# Revit family: Hitachi_RAS-50YHA3_RAS-60YHA3_VER2_0813
name_source: partatom
category: Mechanical Equipment
revit_build: Autodesk Revit 2013 (Build: 20120221_2030(x64)
units: mm (PartAtom-declared; Revit-internal decimal feet)

## types (2) — shared parameters
Dehumidifying Capacity = 2.8 l/h
Depth = 207 mm  [stored 0.679134 ft]
Height = 295 mm  [stored 0.967848 ft]
Manufacturer = Hitachi
Pip Connection Size - Liquid = 6.40 mm
Pipe Connection Size - Gas = 12.70 mm
Pipe Length (min./max.) = 3m to 30m
URL = www.temperzone.biz
Weight (kg) = 11
Width = 1030 mm  [stored 3.37927 ft]

## per-type parameters (varying)
| type | Cooling Capacity | Cooling Range (kW) | Description | Energy Star | Heating Capacity | Heating Range (kW) | Model - Outdoor | Pipe Height (max.) |
| RAS-60YHA3 | 6 kW | 0.9 kW to 6.8 kW | Hitachi Wall Mounted 6.0kW Heatpump RAS-60YHA3 | No | 7 kW | 0.9 kW to 7.5 kW | RAC-60YHA3 | 20m |
| RAS-50YHA3 | 5 kW | 0.9 kW to 5.8 kW | Hitachi Wall Mounted 5.0kW Heatpump RAS-50YHA3 | Yes | 6 kW | 0.9 kW to 6.8 kW | RAC-50YHA3 | 10m |

note: column(s) folded — value = type name in every type: Model

note: [stored X ft] marks values corroborated as IEEE doubles in the binary element streams (Revit-internal decimal feet)

## geometry (parser evidence)
native form markers: Blend x4, Sweep x3
no freeform markers — native parametric forms only
